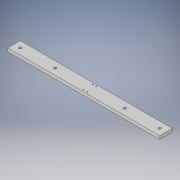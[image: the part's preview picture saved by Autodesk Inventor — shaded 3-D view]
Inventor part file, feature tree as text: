
AUTODESK INVENTOR PART (.ipt)
format: ipt  version: 2018 (Build 220112000, 112)  size: 115,200 bytes
history: native  units: in
note: dims shown in document units (in); Inventor stores cm internally (conversion verified against a paired STEP export)
features: sketch x3, hole x2, extrude x1
ambient origin geometry x8: Origin, YZ Plane, XZ Plane, XY Plane, X Axis, Y Axis, Z Axis, Center Point
bodies: Solid1 (feature_tree)
feature tree (6):
  extrude  "Extrusion1"  Depth=2.0in
  hole  "Hole1"  [1 undecoded]
  hole  "Hole2"  [1 undecoded]
  sketch  "Sketch1"  dims[d0=24.0in d1=2.0in]
  sketch  "Sketch2"  dims[d2=0.5in d3=0.0in d4=11.0in]
  sketch  "Sketch3"  dims[d5=5.5in d6=0.397in d7=0.75in d8=0.635in d9=0.25in d10=0.5635in d11=1.0in d12=0.8108in d13=0.575in d14=1.43in d15=0.156in d16=0.38in d17=0.385in d18=0.25in d19=0.5635in d20=0.536in d21=0.8108in]
note: 2 required parameter values undecoded (feature->parameter linkage not recoverable at this tier; creation-order binding heuristic only, values carry confidence <= 0.55)
